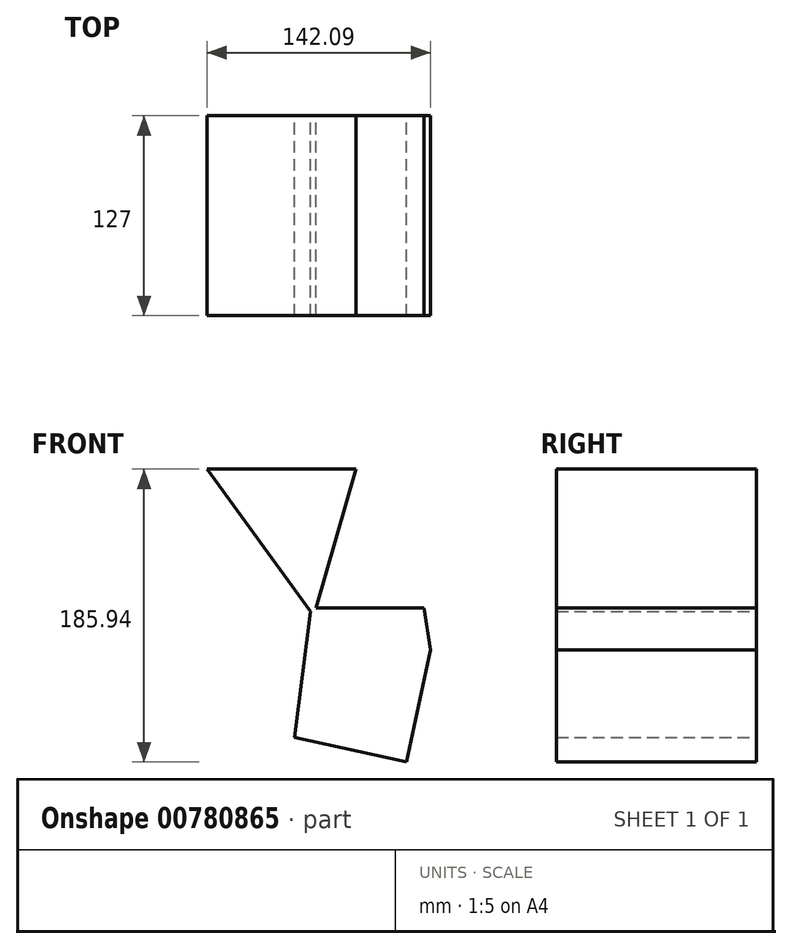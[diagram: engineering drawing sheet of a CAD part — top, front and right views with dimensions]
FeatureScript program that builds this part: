
annotation { "Feature Type Name" : "Feature", "Feature Type Description" : "" }
export const myFeature = defineFeature(function(context is Context, id is Id, definition is map)
    precondition{}
    {
        {
            var Q0;
            Q0=qCreatedBy(makeId("Front.planeOp"),FACE);
            var sketch = newSketch(context, id + "F0", { "sketchPlane" : qUnion([Q0])});
            skLineSegment(sketch, "E0", {"start": v(-25.52, 42.06) * mm, "end": v(43.08, 42.06) * mm});
            skLineSegment(sketch, "E1", {"start": v(43.08, 42.06) * mm, "end": v(47.42, 15.26) * mm});
            skLineSegment(sketch, "E2", {"start": v(47.42, 15.26) * mm, "end": v(32.1, -55.7) * mm});
            skLineSegment(sketch, "E3", {"start": v(32.1, -55.7) * mm, "end": v(-39.15, -40.32) * mm});
            skLineSegment(sketch, "E4", {"start": v(-39.15, -40.32) * mm, "end": v(-28.81, 39.87) * mm});
            skLineSegment(sketch, "E5", {"start": v(-28.81, 39.87) * mm, "end": v(-94.67, 130.24) * mm});
            skLineSegment(sketch, "E6", {"start": v(-94.67, 130.24) * mm, "end": v(0, 130.24) * mm});
            skLineSegment(sketch, "E7", {"start": v(0, 130.24) * mm, "end": v(-25.52, 42.06) * mm});
            skSolve(sketch);
        }
        {
            var Q0;
            Q0=makeQuery(id+"F0.imprint","IMPRINT",FACE,{"disambiguationData":[TD([[makeQuery(id+"F0.imprint","IMPRINT",EDGE,{"derivedFrom":sQuery(id+"F0.wireOp",EDGE,"E0")}),-1.0]])]});
            extrude(context, id + "F1", {"entities" : qUnion([Q0]), "depth" : 127 * mm, "offsetDistance" : 25.4 * mm});
        }
    });
